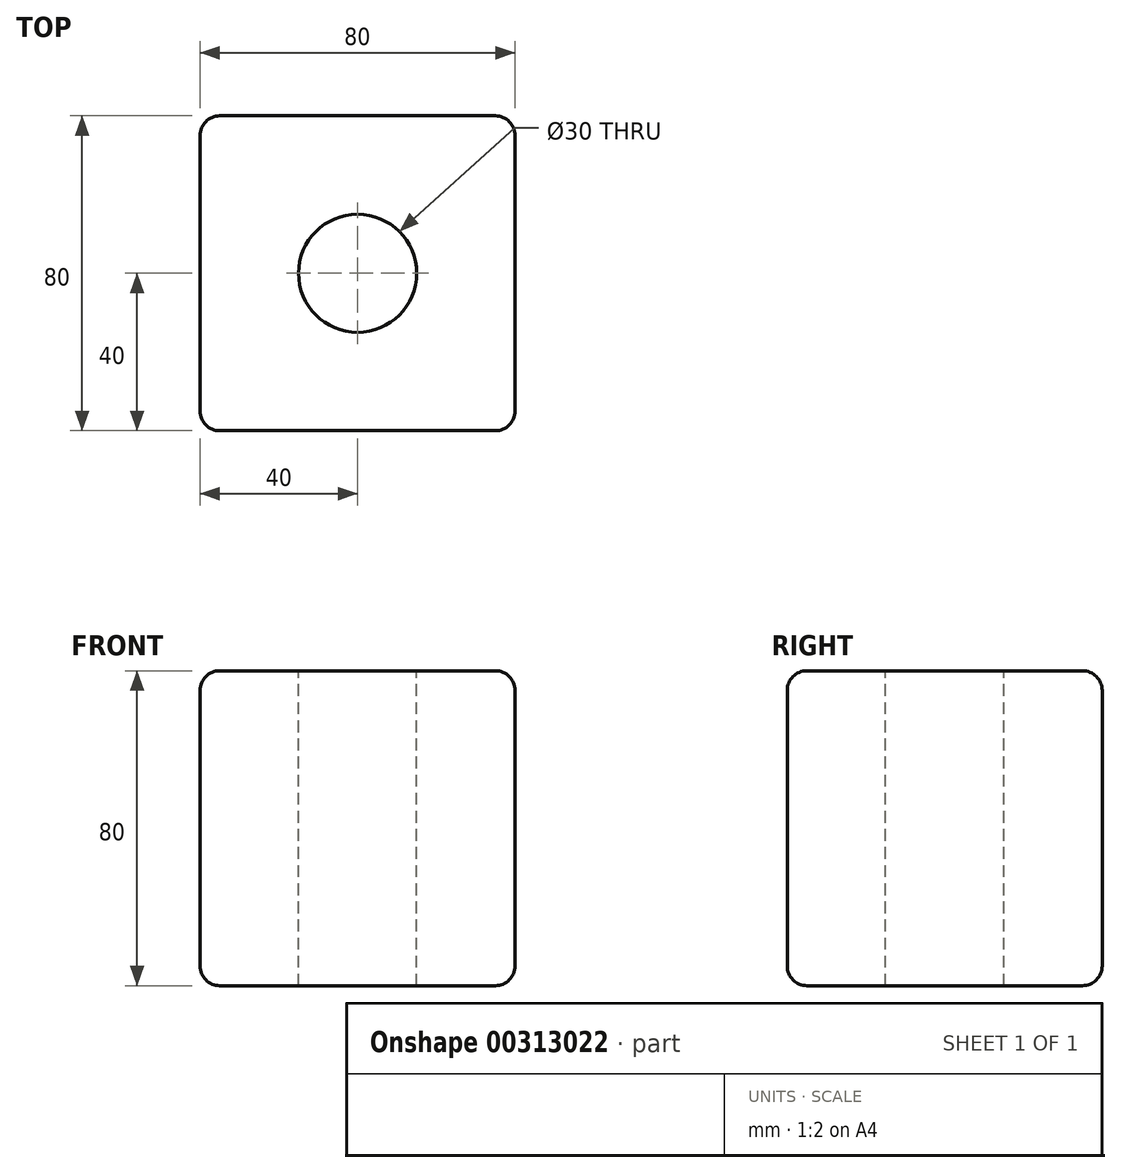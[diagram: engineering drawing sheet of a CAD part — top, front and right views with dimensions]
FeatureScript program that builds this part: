
annotation { "Feature Type Name" : "Feature", "Feature Type Description" : "" }
export const myFeature = defineFeature(function(context is Context, id is Id, definition is map)
    precondition{}
    {
        {
            var Q0;
            Q0=qCreatedBy(makeId("Top.planeOp"),FACE);
            var sketch = newSketch(context, id + "F0", { "sketchPlane" : qUnion([Q0])});
            skLineSegment(sketch, "E0.bottom", {"start": v(-40, 40) * mm, "end": v(40, 40) * mm});
            skLineSegment(sketch, "E0.top", {"start": v(-40, -40) * mm, "end": v(40, -40) * mm});
            skLineSegment(sketch, "E0.left", {"start": v(-40, 40) * mm, "end": v(-40, -40) * mm});
            skLineSegment(sketch, "E0.right", {"start": v(40, 40) * mm, "end": v(40, -40) * mm});
            skPoint(sketch, "E0.middle", {"position": v(0, 0) * mm});
            skSolve(sketch);
        }
        {
            var Q0;
            Q0=makeQuery(id+"F0.imprint","IMPRINT",FACE,{"disambiguationData":[TD([[makeQuery(id+"F0.imprint","IMPRINT",EDGE,{"derivedFrom":sQuery(id+"F0.wireOp",EDGE,"E0.bottom")}),-1.0]])]});
            extrude(context, id + "F1", {"entities" : qUnion([Q0]), "depth" : 80 * mm});
        }
        {
            var Q0;
            Q0=makeQuery(id+"F1.opExtrude","CAP_EDGE",EDGE,{"disambiguationData":[OSD([sQuery(id+"F0.wireOp",EDGE,"E0.bottom")])],"isStart":false});
            var Q1;
            Q1=makeQuery(id+"F1.opExtrude","CAP_EDGE",EDGE,{"disambiguationData":[OSD([sQuery(id+"F0.wireOp",EDGE,"E0.left")])],"isStart":false});
            var Q2;
            Q2=makeQuery(id+"F1.opExtrude","CAP_EDGE",EDGE,{"disambiguationData":[OSD([sQuery(id+"F0.wireOp",EDGE,"E0.right")])],"isStart":false});
            var Q3;
            Q3=makeQuery(id+"F1.opExtrude","CAP_EDGE",EDGE,{"disambiguationData":[OSD([sQuery(id+"F0.wireOp",EDGE,"E0.top")])],"isStart":false});
            var Q4;
            Q4=makeQuery(id+"F1.opExtrude","SWEPT_EDGE",EDGE,{"disambiguationData":[OSD([sQuery(id+"F0.wireOp",EDGE,"E0.bottom"),sQuery(id+"F0.wireOp",EDGE,"E0.left")])]});
            var Q5;
            Q5=makeQuery(id+"F1.opExtrude","CAP_EDGE",EDGE,{"disambiguationData":[OSD([sQuery(id+"F0.wireOp",EDGE,"E0.left")])],"isStart":true});
            var Q6;
            Q6=makeQuery(id+"F1.opExtrude","SWEPT_EDGE",EDGE,{"disambiguationData":[OSD([sQuery(id+"F0.wireOp",EDGE,"E0.top"),sQuery(id+"F0.wireOp",EDGE,"E0.left")])]});
            var Q7;
            Q7=makeQuery(id+"F1.opExtrude","SWEPT_EDGE",EDGE,{"disambiguationData":[OSD([sQuery(id+"F0.wireOp",EDGE,"E0.top"),sQuery(id+"F0.wireOp",EDGE,"E0.right")])]});
            var Q8;
            Q8=makeQuery(id+"F1.opExtrude","SWEPT_FACE",FACE,{"disambiguationData":[OSD([sQuery(id+"F0.wireOp",EDGE,"E0.top")])]});
            var Q9;
            Q9=makeQuery(id+"F1.opExtrude","SWEPT_FACE",FACE,{"disambiguationData":[OSD([sQuery(id+"F0.wireOp",EDGE,"E0.bottom")])]});
            fillet(context, id + "F2", {"entities" : qUnion([Q0, Q1, Q2, Q3, Q4, Q5, Q6, Q7, Q8, Q9]), "radius" : 5 * mm, "tangentPropagation" : true, "allowEdgeOverflow" : false});
        }
        {
            var Q0;
            {var subQ0=sQuery(id+"F0.wireOp",EDGE,"E0.top");Q0=makeQuery(id+"F2.opFillet","BLEND_FACE",FACE,{"disambiguationData":[OSD([subQ0]),TDD([makeQuery(id+"F1.opExtrude","CAP_EDGE",EDGE,{"disambiguationData":[OSD([subQ0])],"isStart":true})])]});}
            var Q1;
            Q1=makeQuery(id+"F1.opExtrude","SWEPT_FACE",FACE,{"disambiguationData":[OSD([sQuery(id+"F0.wireOp",EDGE,"E0.right")])]});
            fillet(context, id + "F3", {"entities" : qUnion([Q0, Q1]), "radius" : 5 * mm, "tangentPropagation" : true, "allowEdgeOverflow" : false});
        }
        {
            var Q0;
            Q0=makeQuery(id+"F1.opExtrude","CAP_FACE",FACE,{"disambiguationData":[OSD([sQuery(id+"F0.wireOp",EDGE,"E0.bottom"),sQuery(id+"F0.wireOp",EDGE,"E0.top"),sQuery(id+"F0.wireOp",EDGE,"E0.left"),sQuery(id+"F0.wireOp",EDGE,"E0.right")])],"isStart":false});
            var sketch = newSketch(context, id + "F4", { "sketchPlane" : qUnion([Q0])});
            skCircle(sketch, "E1", {"center": v(0, 0) * mm, "radius": 15 * mm});
            skSolve(sketch);
        }
        {
            var Q0;
            Q0 = qSketchRegion(id + "F4", true);
            extrude(context, id + "F5", {"entities" : qUnion([Q0]), "operationType" : NewBodyOperationType.REMOVE, "endBound" : BoundingType.THROUGH_ALL, "oppositeDirection" : true, "depth" : 25 * mm});
        }
    });
